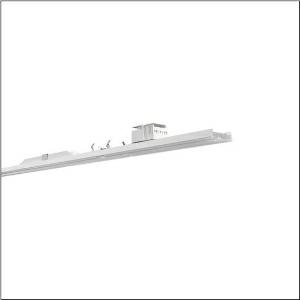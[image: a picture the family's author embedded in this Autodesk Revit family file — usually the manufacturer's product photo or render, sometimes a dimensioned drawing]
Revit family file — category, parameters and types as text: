
# Revit family: licross_r__11_recessed_mo_51tl1edn485f_243d
name_source: partatom
category: Lighting Fixtures
units: mm (PartAtom-declared; Revit-internal decimal feet)

## family parameters
Cut with Voids When Loaded = No
Host = Face
Light Source = No
Part Type = Normal
Room Calculation Point = No
Round Connector Dimension = Use Diameter
Shared = No

## types (1)
- --- (1 x LED, 8750 lm, 55.4 W, 4000K)
    Apparent Load = 55 VA
    CIE Flux Codes = 85 95 99 100 100
    Color Rendering = 80
    Color Temperature = 4000K
    Default Elevation = 1800 mm
    Description = Licross® 11 Recessed MO, luminaire insert, of sheet steel, galvanised, coil coated, white, length: 1.500mm, width: 66mm, height: 67mm, LED rated luminous flux: 8.750lm, light colour: 840, control gear: DALI 2, control gear: ECG DALI, with plug, 5-pole, with phase selection, mains connection: 220..240V, AC, 50/60Hz, halogen-free wiring, primary optical cover: cover, of PMMA, light emission: direct distribution, protection rating (complete): IP40, insulation class (complete): insulation class I (protective earthing), certification: CE, ENEC, VDE, UKCA, protection symbol: D if used in an environment without relevant dust loads with corresponding accessories, permissible ambient temperature for indoor applications: -25..+40°C, reducing of maximum allowable ambient temperature of 5°C with ceiling mounting, corresponds to IFS (International Featured Standards) requirements for safety and quality in the food industry, LABS conformity tested according to VDMA 24364:2018-05, packaging unit: 1 piece
    Height = 58 mm
    Lamp = 1 x LED
    Lamp Light Flux = 8750 lm
    Lamp Power = 55.4 W
    Lamp count = 1
    Length = 1500 mm
    Luminous efficacy = 158 lm/W
    Manufacturer = Siteco
    ModVariant = No
    Model = 51TL1EDN485F
    Mounting Place = Ceiling
    Mounting Type = Pendant
    Number of Poles = 1
    OnlyDefault = Yes
    Power Factor = 1
    Product Name = Licross® 11 Recessed MO
    Product group = luminaire insert
    ProductGroupID = 902
    Protection Class = Protection class I
    Protection Degree = IP 40
    RLX_Detail_Level = 1
    RlxData = <blob elided: 22549 chars, md5=9f8ac6d2>
    Socket = socket
    Standby Power = 0 W
    System Light Flux = 8750 lm
    System Power = 55 W
    Type Comments = factory setting: luminous flux: 100 % | dim-lin: 254 | 365 mA
    Type Image = l_1266722.jpg
    URL = http://relux.com
    VarID = @adj_093093
    Voltage = 0 V
    Weight = 0.00 kg
    Width = 66 mm

## geometry (parser evidence)
native form markers: Blend x4, Sweep x10
no freeform markers — native parametric forms only
